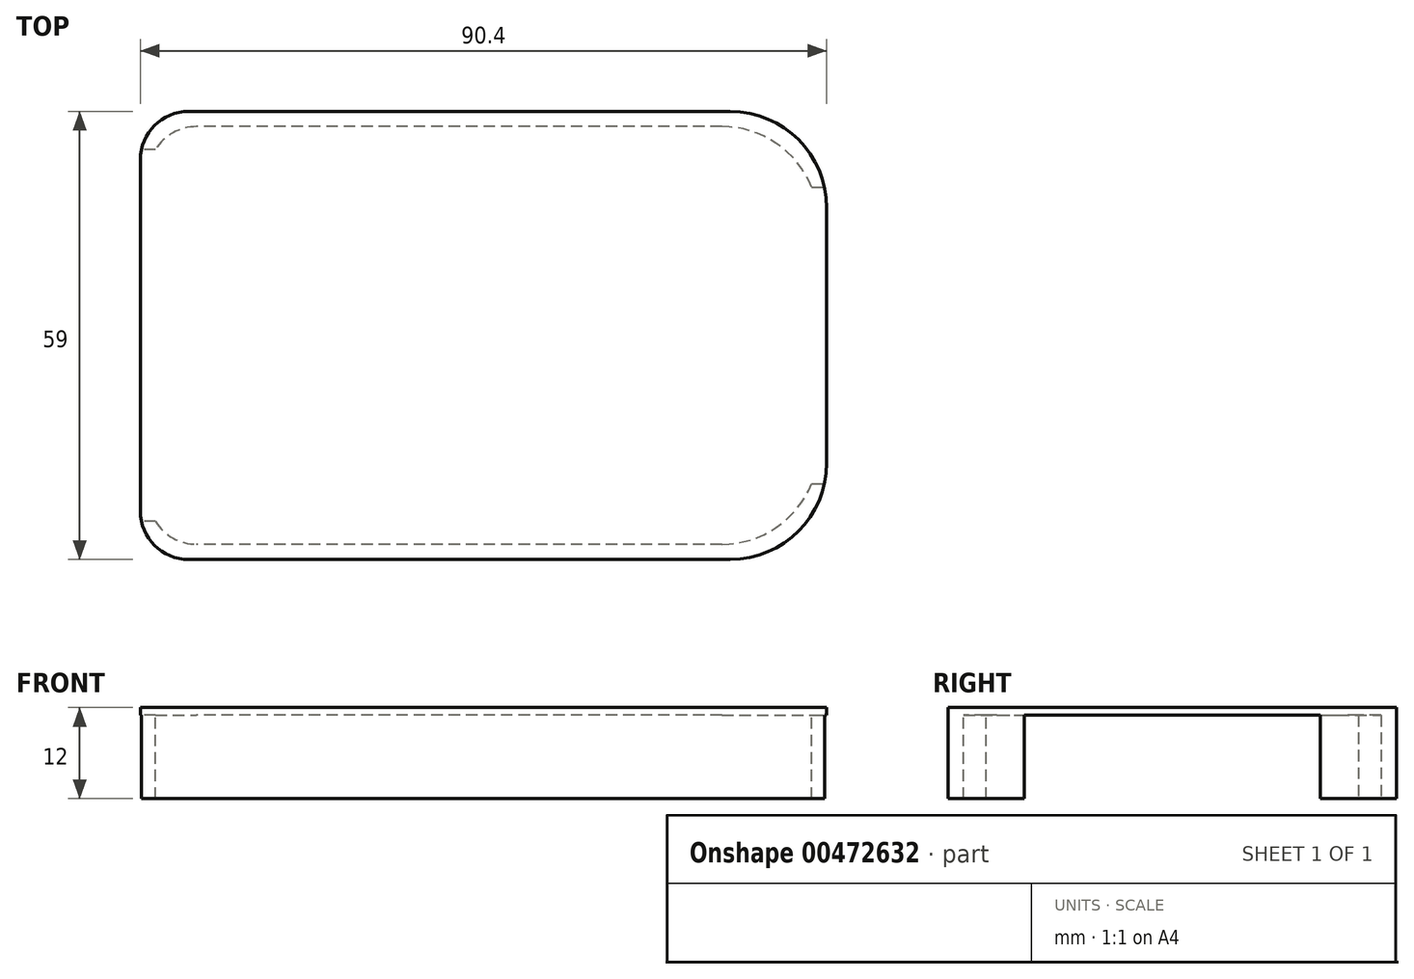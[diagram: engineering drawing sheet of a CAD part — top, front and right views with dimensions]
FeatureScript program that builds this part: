
annotation { "Feature Type Name" : "Feature", "Feature Type Description" : "" }
export const myFeature = defineFeature(function(context is Context, id is Id, definition is map)
    precondition{}
    {
        {
            var Q0;
            Q0=qCreatedBy(makeId("Top.planeOp"),FACE);
            var sketch = newSketch(context, id + "F0", { "sketchPlane" : qUnion([Q0])});
            skLineSegment(sketch, "E0.bottom", {"start": v(43.2, -27.5) * mm, "end": v(-43.2, -27.5) * mm});
            skLineSegment(sketch, "E0.top", {"start": v(43.2, 27.5) * mm, "end": v(-43.2, 27.5) * mm});
            skLineSegment(sketch, "E0.left", {"start": v(43.2, -27.5) * mm, "end": v(43.2, 27.5) * mm});
            skLineSegment(sketch, "E0.right", {"start": v(-43.2, -27.5) * mm, "end": v(-43.2, 27.5) * mm});
            skPoint(sketch, "E0.middle", {"position": v(0, 0) * mm});
            skLineSegment(sketch, "E1.0", {"start": v(-45.2, -29.5) * mm, "end": v(-45.2, 29.5) * mm});
            skLineSegment(sketch, "E1.1", {"start": v(45.2, -29.5) * mm, "end": v(-45.2, -29.5) * mm});
            skLineSegment(sketch, "E1.2", {"start": v(45.2, -29.5) * mm, "end": v(45.2, 29.5) * mm});
            skLineSegment(sketch, "E1.3", {"start": v(45.2, 29.5) * mm, "end": v(-45.2, 29.5) * mm});
            skLineSegment(sketch, "E2", {"start": v(-43.2, -24.5) * mm, "end": v(-45.2, -24.5) * mm});
            skLineSegment(sketch, "E3", {"start": v(-43.2, 24.5) * mm, "end": v(-45.2, 24.5) * mm});
            skLineSegment(sketch, "E4", {"start": v(43.2, -19.5) * mm, "end": v(45.2, -19.5) * mm});
            skLineSegment(sketch, "E5", {"start": v(43.2, 19.5) * mm, "end": v(45.2, 19.5) * mm});
            skSolve(sketch);
        }
        {
            var Q0;
            Q0=makeQuery(id+"F0.imprint","IMPRINT",FACE,{"disambiguationData":[TD([[makeQuery(id+"F0.imprint","IMPRINT",EDGE,{"derivedFrom":sQuery(id+"F0.wireOp",EDGE,"E0.bottom")}),-1.0]])]});
            var Q1;
            Q1=makeQuery(id+"F0.imprint","IMPRINT",FACE,{"disambiguationData":[TD([[makeQuery(id+"F0.imprint","IMPRINT",EDGE,{"derivedFrom":sQuery(id+"F0.wireOp",EDGE,"E0.right")}),1.0]])]});
            var Q2;
            Q2=makeQuery(id+"F0.imprint","IMPRINT",FACE,{"disambiguationData":[TD([[makeQuery(id+"F0.imprint","IMPRINT",EDGE,{"derivedFrom":sQuery(id+"F0.wireOp",EDGE,"E0.left")}),-1.0]])]});
            extrude(context, id + "F1", {"entities" : qUnion([Q0, Q1, Q2]), "oppositeDirection" : true, "depth" : 1 * mm});
        }
        {
            var Q0;
            Q0=makeQuery(id+"F0.imprint","IMPRINT",FACE,{"disambiguationData":[TD([[makeQuery(id+"F0.imprint","IMPRINT",EDGE,{"derivedFrom":sQuery(id+"F0.wireOp",EDGE,"E0.bottom")}),1.0]])]});
            var Q1;
            Q1=makeQuery(id+"F0.imprint","IMPRINT",FACE,{"disambiguationData":[TD([[makeQuery(id+"F0.imprint","IMPRINT",EDGE,{"derivedFrom":sQuery(id+"F0.wireOp",EDGE,"E0.top")}),-1.0]])]});
            extrude(context, id + "F2", {"entities" : qUnion([Q0, Q1]), "operationType" : NewBodyOperationType.ADD, "oppositeDirection" : true, "depth" : 12 * mm});
        }
        {
            var Q0;
            Q0=makeQuery(id+"F2.opExtrude","SWEPT_EDGE",EDGE,{"disambiguationData":[OSD([sQuery(id+"F0.wireOp",EDGE,"E0.bottom"),sQuery(id+"F0.wireOp",EDGE,"E0.right")])]});
            var Q1;
            Q1=makeQuery(id+"F2.opExtrude","SWEPT_EDGE",EDGE,{"disambiguationData":[OSD([sQuery(id+"F0.wireOp",EDGE,"E1.0"),sQuery(id+"F0.wireOp",EDGE,"E1.1")])]});
            var Q2;
            Q2=makeQuery(id+"F2.opExtrude","SWEPT_EDGE",EDGE,{"disambiguationData":[OSD([sQuery(id+"F0.wireOp",EDGE,"E0.top"),sQuery(id+"F0.wireOp",EDGE,"E0.right")])]});
            var Q3;
            Q3=makeQuery(id+"F2.opExtrude","SWEPT_EDGE",EDGE,{"disambiguationData":[OSD([sQuery(id+"F0.wireOp",EDGE,"E1.0"),sQuery(id+"F0.wireOp",EDGE,"E1.3")])]});
            fillet(context, id + "F3", {"entities" : qUnion([Q0, Q1, Q2, Q3]), "radius" : 6.37 * mm, "tangentPropagation" : true, "allowEdgeOverflow" : false});
        }
        {
            var Q0;
            Q0=makeQuery(id+"F2.opExtrude","SWEPT_EDGE",EDGE,{"disambiguationData":[OSD([sQuery(id+"F0.wireOp",EDGE,"E0.top"),sQuery(id+"F0.wireOp",EDGE,"E0.left")])]});
            var Q1;
            Q1=makeQuery(id+"F2.opExtrude","SWEPT_EDGE",EDGE,{"disambiguationData":[OSD([sQuery(id+"F0.wireOp",EDGE,"E0.bottom"),sQuery(id+"F0.wireOp",EDGE,"E0.left")])]});
            var Q2;
            Q2=makeQuery(id+"F2.opExtrude","SWEPT_EDGE",EDGE,{"disambiguationData":[OSD([sQuery(id+"F0.wireOp",EDGE,"E1.1"),sQuery(id+"F0.wireOp",EDGE,"E1.2")])]});
            var Q3;
            Q3=makeQuery(id+"F2.opExtrude","SWEPT_EDGE",EDGE,{"disambiguationData":[OSD([sQuery(id+"F0.wireOp",EDGE,"E1.2"),sQuery(id+"F0.wireOp",EDGE,"E1.3")])]});
            fillet(context, id + "F4", {"entities" : qUnion([Q0, Q1, Q2, Q3]), "radius" : 12.7 * mm, "tangentPropagation" : true, "allowEdgeOverflow" : false});
        }
    });
